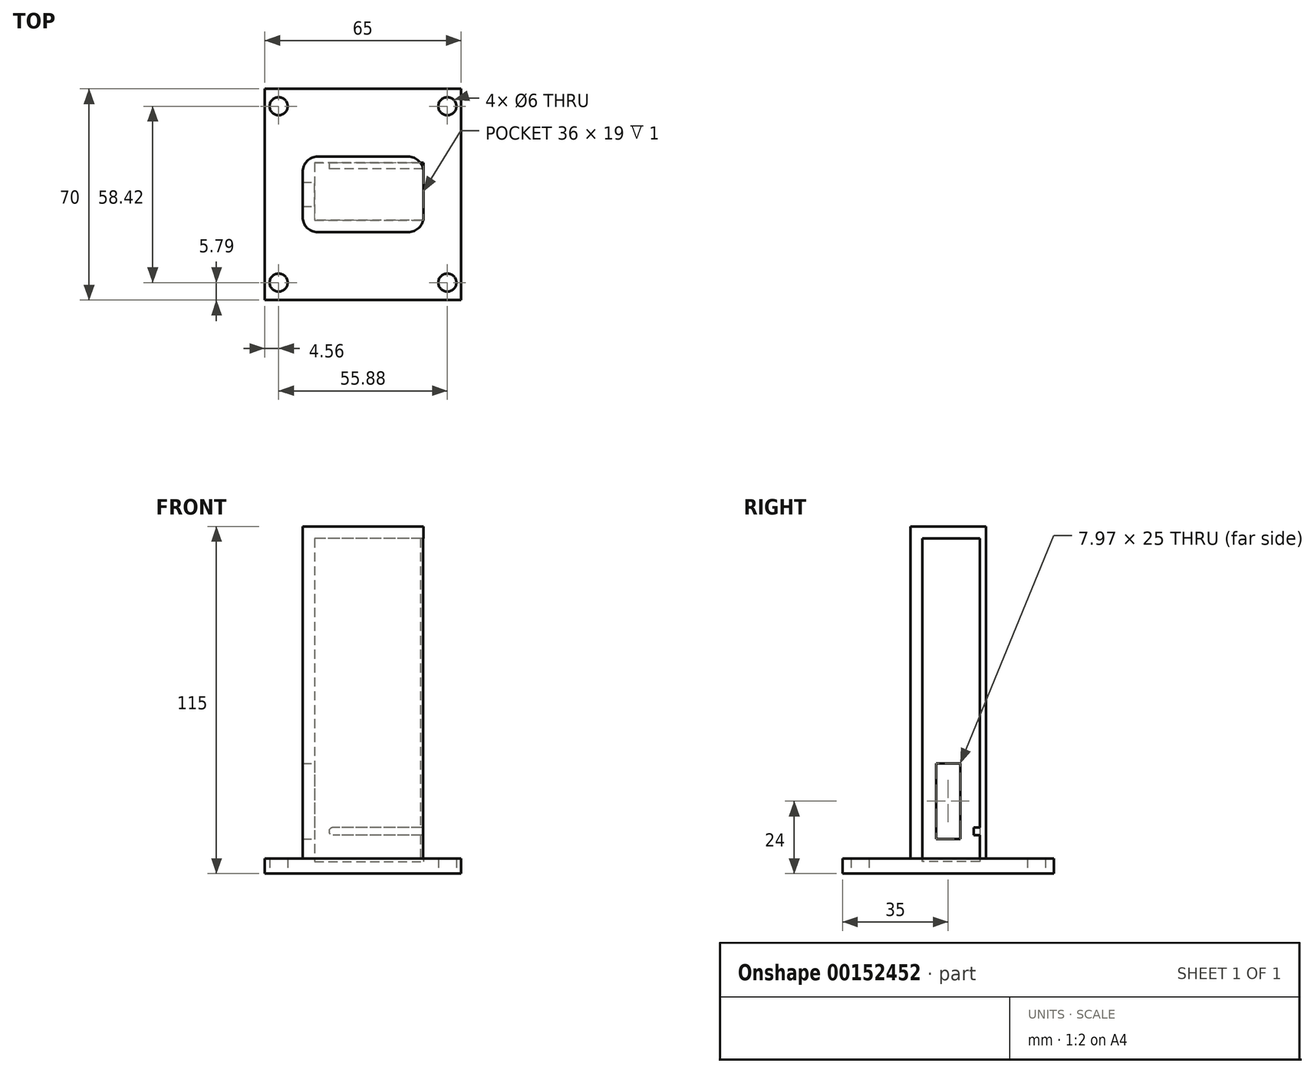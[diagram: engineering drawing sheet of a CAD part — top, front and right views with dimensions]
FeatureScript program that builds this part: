
annotation { "Feature Type Name" : "Feature", "Feature Type Description" : "" }
export const myFeature = defineFeature(function(context is Context, id is Id, definition is map)
    precondition{}
    {
        {
            var Q0;
            Q0=qCreatedBy(makeId("Top.planeOp"),FACE);
            var sketch = newSketch(context, id + "F0", { "sketchPlane" : qUnion([Q0])});
            skLineSegment(sketch, "E0.bottom", {"start": v(32.5, 35) * mm, "end": v(-32.5, 35) * mm});
            skLineSegment(sketch, "E0.top", {"start": v(32.5, -35) * mm, "end": v(-32.5, -35) * mm});
            skLineSegment(sketch, "E0.left", {"start": v(32.5, 35) * mm, "end": v(32.5, -35) * mm});
            skLineSegment(sketch, "E0.right", {"start": v(-32.5, 35) * mm, "end": v(-32.5, -35) * mm});
            skPoint(sketch, "E0.middle", {"position": v(0, 0) * mm});
            skSolve(sketch);
        }
        {
            var Q0;
            Q0=makeQuery(id+"F0.imprint","IMPRINT",FACE,{"disambiguationData":[TD([[makeQuery(id+"F0.imprint","IMPRINT",EDGE,{"derivedFrom":sQuery(id+"F0.wireOp",EDGE,"E0.bottom")}),1.0]])]});
            extrude(context, id + "F1", {"entities" : qUnion([Q0]), "depth" : 5 * mm});
        }
        {
            var Q0;
            Q0=makeQuery(id+"F1.opExtrude","CAP_FACE",FACE,{"disambiguationData":[OSD([sQuery(id+"F0.wireOp",EDGE,"E0.bottom"),sQuery(id+"F0.wireOp",EDGE,"E0.top"),sQuery(id+"F0.wireOp",EDGE,"E0.left"),sQuery(id+"F0.wireOp",EDGE,"E0.right")])],"isStart":false});
            var sketch = newSketch(context, id + "F2", { "sketchPlane" : qUnion([Q0])});
            skLineSegment(sketch, "E1.bottom", {"start": v(20, -12.5) * mm, "end": v(-20, -12.5) * mm});
            skLineSegment(sketch, "E1.top", {"start": v(20, 12.5) * mm, "end": v(-20, 12.5) * mm});
            skLineSegment(sketch, "E1.left", {"start": v(20, -12.5) * mm, "end": v(20, 12.5) * mm});
            skLineSegment(sketch, "E1.right", {"start": v(-20, -12.5) * mm, "end": v(-20, 12.5) * mm});
            skPoint(sketch, "E1.middle", {"position": v(0, 0) * mm});
            skSolve(sketch);
        }
        {
            var Q0;
            Q0=makeQuery(id+"F2.imprint","IMPRINT",FACE,{"disambiguationData":[TD([[makeQuery(id+"F2.imprint","IMPRINT",EDGE,{"derivedFrom":sQuery(id+"F2.wireOp",EDGE,"E1.bottom")}),-1.0]])]});
            extrude(context, id + "F3", {"entities" : qUnion([Q0]), "operationType" : NewBodyOperationType.ADD, "depth" : 110 * mm});
        }
        {
            var Q0;
            Q0=makeQuery(id+"F1.opExtrude","CAP_FACE",FACE,{"disambiguationData":[OSD([sQuery(id+"F0.wireOp",EDGE,"E0.bottom"),sQuery(id+"F0.wireOp",EDGE,"E0.top"),sQuery(id+"F0.wireOp",EDGE,"E0.left"),sQuery(id+"F0.wireOp",EDGE,"E0.right")])],"isStart":true});
            var sketch = newSketch(context, id + "F4", { "sketchPlane" : qUnion([Q0])});
            skLineSegment(sketch, "E2.bottom", {"start": v(27.94, -29.2) * mm, "end": v(-27.94, -29.21) * mm});
            skLineSegment(sketch, "E2.top", {"start": v(27.94, 29.21) * mm, "end": v(-27.94, 29.2) * mm});
            skLineSegment(sketch, "E2.left", {"start": v(27.94, -29.2) * mm, "end": v(27.94, 29.21) * mm});
            skLineSegment(sketch, "E2.right", {"start": v(-27.94, -29.21) * mm, "end": v(-27.94, 29.2) * mm});
            skPoint(sketch, "E2.middle", {"position": v(0, 0) * mm});
            skSolve(sketch);
        }
        {
            var Q0;
            Q0=sQuery(id+"F4.wireOp",VERTEX,"E2.right.end");
            var Q1;
            Q1=sQuery(id+"F4.wireOp",VERTEX,"E2.top.start");
            var Q2;
            Q2=sQuery(id+"F4.wireOp",VERTEX,"E2.left.start");
            var Q3;
            Q3=sQuery(id+"F4.wireOp",VERTEX,"E2.right.start");
            var Q4;
            Q4=makeQuery(id+"F1.opExtrude","SWEPT_BODY",BODY,{"disambiguationData":[OSD([sQuery(id+"F0.wireOp",EDGE,"E0.bottom"),sQuery(id+"F0.wireOp",EDGE,"E0.top"),sQuery(id+"F0.wireOp",EDGE,"E0.left"),sQuery(id+"F0.wireOp",EDGE,"E0.right")])]});
            hole(context, id + "F5", {"style" : HoleStyle.SIMPLE, "endStyle" : HoleEndStyle.THROUGH, "holeDiameter" : 6 * mm, "locations" : qUnion([Q0, Q1, Q2, Q3]), "scope" : qUnion([Q4]), "isTappedThrough" : true});
        }
        {
            var Q0;
            Q0=makeQuery(id+"F3.opExtrude","SWEPT_FACE",FACE,{"disambiguationData":[OSD([sQuery(id+"F2.wireOp",EDGE,"E1.left")])]});
            shell(context, id + "F6", {"entities" : qUnion([Q0]), "thickness" : 4 * mm});
        }
        {
            var Q0;
            Q0=makeQuery(id+"F6.opShell","OFFSET_FACE",FACE,{"disambiguationData":[OSD([sQuery(id+"F2.wireOp",EDGE,"E1.right")])]});
            var sketch = newSketch(context, id + "F7", { "sketchPlane" : qUnion([Q0])});
            skLineSegment(sketch, "E3.bottom", {"start": v(-3.98, 36.5) * mm, "end": v(3.98, 36.5) * mm});
            skLineSegment(sketch, "E3.top", {"start": v(-3.98, 11.5) * mm, "end": v(3.98, 11.5) * mm});
            skLineSegment(sketch, "E3.left", {"start": v(-3.98, 36.5) * mm, "end": v(-3.98, 11.5) * mm});
            skLineSegment(sketch, "E3.right", {"start": v(3.98, 36.5) * mm, "end": v(3.98, 11.5) * mm});
            skPoint(sketch, "E3.middle", {"position": v(0, 24) * mm});
            skPoint(sketch, "E3.middle.positionSnap0", {"position": v(0, 4) * mm});
            skPoint(sketch, "E3.centerSnap0", {"position": v(0, 4) * mm});
            skSolve(sketch);
        }
        {
            var Q0;
            Q0=makeQuery(id+"F7.imprint","IMPRINT",FACE,{"disambiguationData":[TD([[makeQuery(id+"F7.imprint","IMPRINT",EDGE,{"derivedFrom":sQuery(id+"F7.wireOp",EDGE,"E3.bottom")}),-1.0]])]});
            extrude(context, id + "F8", {"entities" : qUnion([Q0]), "operationType" : NewBodyOperationType.REMOVE, "oppositeDirection" : true, "depth" : 25 * mm});
        }
        {
            var Q0;
            Q0=makeQuery(id+"F6.opShell","OFFSET_FACE",FACE,{"disambiguationData":[OSD([sQuery(id+"F2.wireOp",EDGE,"E1.top")])]});
            var sketch = newSketch(context, id + "F9", { "sketchPlane" : qUnion([Q0])});
            skLineSegment(sketch, "E4", {"start": v(20, 14) * mm, "end": v(-10, 14) * mm});
            skArc(sketch, "E5.0.startCap", {"start": v(20, 15.25) * mm, "mid": v(21.25, 14) * mm, "end": v(20, 12.75) * mm});
            skArc(sketch, "E5.0.endCap", {"start": v(-10, 12.75) * mm, "mid": v(-11.25, 14) * mm, "end": v(-10, 15.25) * mm});
            skLineSegment(sketch, "E5.0.left", {"start": v(20, 12.75) * mm, "end": v(-10, 12.75) * mm});
            skLineSegment(sketch, "E5.0.right", {"start": v(20, 15.25) * mm, "end": v(-10, 15.25) * mm});
            skSolve(sketch);
        }
        {
            var Q0;
            Q0=makeQuery(id+"F9.imprint","IMPRINT",FACE,{"disambiguationData":[TD([[makeQuery(id+"F9.imprint","IMPRINT",EDGE,{"derivedFrom":sQuery(id+"F9.wireOp",EDGE,"E5.0.endCap")}),-1.0]])]});
            extrude(context, id + "F10", {"entities" : qUnion([Q0]), "operationType" : NewBodyOperationType.REMOVE, "oppositeDirection" : true, "depth" : 2 * mm});
        }
        {
            var Q0;
            Q0=makeQuery(id+"F3.opExtrude","SWEPT_EDGE",EDGE,{"disambiguationData":[OSD([sQuery(id+"F2.wireOp",EDGE,"E1.bottom"),sQuery(id+"F2.wireOp",EDGE,"E1.right")])]});
            var Q1;
            Q1=makeQuery(id+"F3.opExtrude","SWEPT_EDGE",EDGE,{"disambiguationData":[OSD([sQuery(id+"F2.wireOp",EDGE,"E1.top"),sQuery(id+"F2.wireOp",EDGE,"E1.right")])]});
            var Q2;
            Q2=makeQuery(id+"F3.opExtrude","SWEPT_EDGE",EDGE,{"disambiguationData":[OSD([sQuery(id+"F2.wireOp",EDGE,"E1.bottom"),sQuery(id+"F2.wireOp",EDGE,"E1.left")])]});
            var Q3;
            Q3=makeQuery(id+"F3.opExtrude","SWEPT_EDGE",EDGE,{"disambiguationData":[OSD([sQuery(id+"F2.wireOp",EDGE,"E1.top"),sQuery(id+"F2.wireOp",EDGE,"E1.left")])]});
            fillet(context, id + "F11", {"entities" : qUnion([Q0, Q1, Q2, Q3]), "radius" : 5 * mm, "tangentPropagation" : true, "allowEdgeOverflow" : false});
        }
    });
